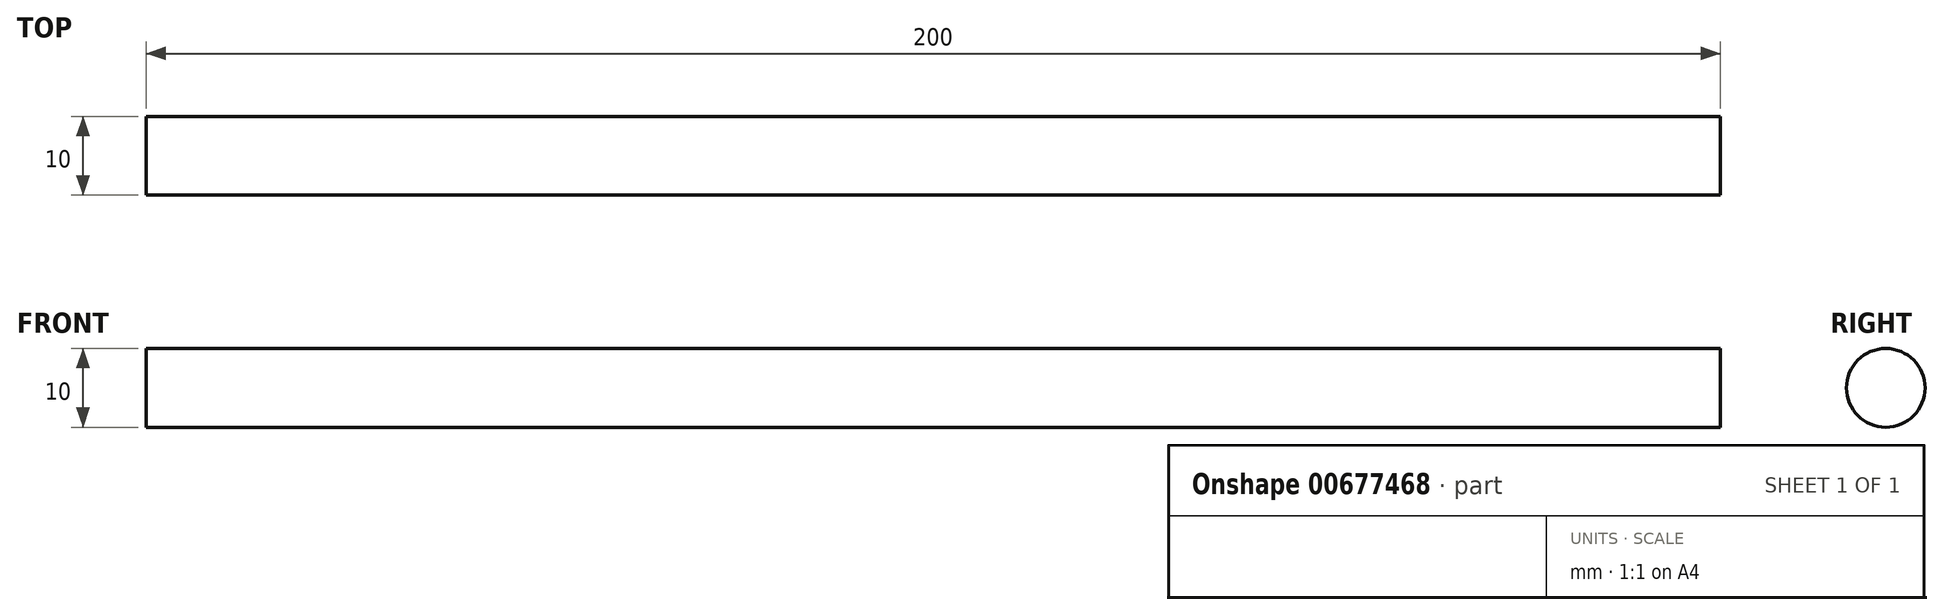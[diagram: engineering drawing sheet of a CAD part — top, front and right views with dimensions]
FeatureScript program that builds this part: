
annotation { "Feature Type Name" : "Feature", "Feature Type Description" : "" }
export const myFeature = defineFeature(function(context is Context, id is Id, definition is map)
    precondition{}
    {
        {
            var Q0;
            Q0=qCreatedBy(makeId("Front.planeOp"),FACE);
            var sketch = newSketch(context, id + "F0", { "sketchPlane" : qUnion([Q0])});
            skLineSegment(sketch, "E0", {"start": v(-100, 0) * mm, "end": v(100, 0) * mm});
            skLineSegment(sketch, "E1", {"start": v(100, 0) * mm, "end": v(100, 5) * mm});
            skLineSegment(sketch, "E2", {"start": v(100, 5) * mm, "end": v(-100, 5) * mm});
            skLineSegment(sketch, "E3", {"start": v(-100, 5) * mm, "end": v(-100, 0) * mm});
            skLineSegment(sketch, "E4", {"start": v(0, 99.3) * mm, "end": v(0, -48.04) * mm, "construction": true});
            skSolve(sketch);
        }
        {
            var Q0;
            Q0 = qSketchRegion(id + "F0", true);
            var Q1;
            Q1=sQuery(id+"F0.wireOp",EDGE,"E0");
            revolve(context, id + "F1", {"entities" : qUnion([Q0]), "axis" : qUnion([Q1]), "revolveType" : RevolveType.FULL});
        }
    });
